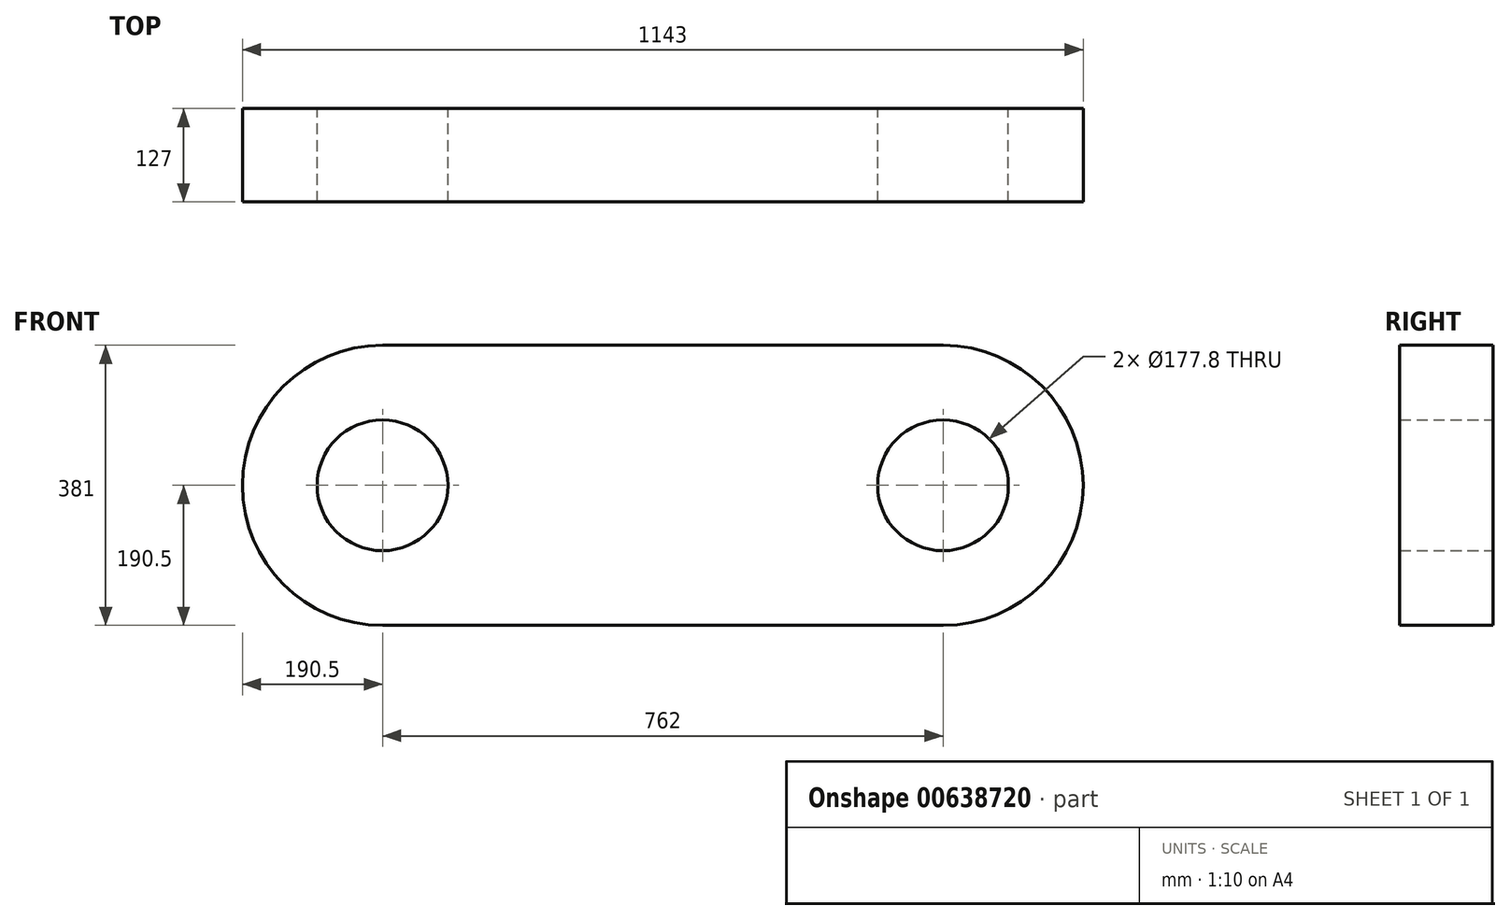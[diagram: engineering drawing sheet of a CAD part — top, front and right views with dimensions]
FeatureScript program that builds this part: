
annotation { "Feature Type Name" : "Feature", "Feature Type Description" : "" }
export const myFeature = defineFeature(function(context is Context, id is Id, definition is map)
    precondition{}
    {
        {
            var Q0;
            Q0=qCreatedBy(makeId("Front.planeOp"),FACE);
            var sketch = newSketch(context, id + "F0", { "sketchPlane" : qUnion([Q0])});
            skArc(sketch, "E0", {"start": v(-381, 190.5) * mm, "mid": v(-571.5, 0) * mm, "end": v(-381, -190.5) * mm});
            skCircle(sketch, "E1", {"center": v(-381, 0) * mm, "radius": 88.9 * mm});
            skLineSegment(sketch, "E2", {"start": v(-381, 190.5) * mm, "end": v(0, 190.5) * mm});
            skLineSegment(sketch, "E3", {"start": v(-381, -190.5) * mm, "end": v(0, -190.5) * mm});
            skArc(sketch, "E4.MirrorCS", {"start": v(381, 190.5) * mm, "mid": v(571.5, 0) * mm, "end": v(381, -190.5) * mm});
            skLineSegment(sketch, "E5.MirrorCS", {"start": v(381, 190.5) * mm, "end": v(0, 190.5) * mm});
            skLineSegment(sketch, "E6.MirrorCS", {"start": v(381, -190.5) * mm, "end": v(0, -190.5) * mm});
            skCircle(sketch, "E7.MirrorC", {"center": v(381, 0) * mm, "radius": 88.9 * mm});
            skSolve(sketch);
        }
        {
            var Q0;
            Q0=makeQuery(id+"F0.imprint","IMPRINT",FACE,{"disambiguationData":[TD([[makeQuery(id+"F0.imprint","IMPRINT",EDGE,{"derivedFrom":sQuery(id+"F0.wireOp",EDGE,"E0")}),1.0]])]});
            extrude(context, id + "F1", {"entities" : qUnion([Q0]), "depth" : 127 * mm, "offsetDistance" : 25.4 * mm});
        }
    });
